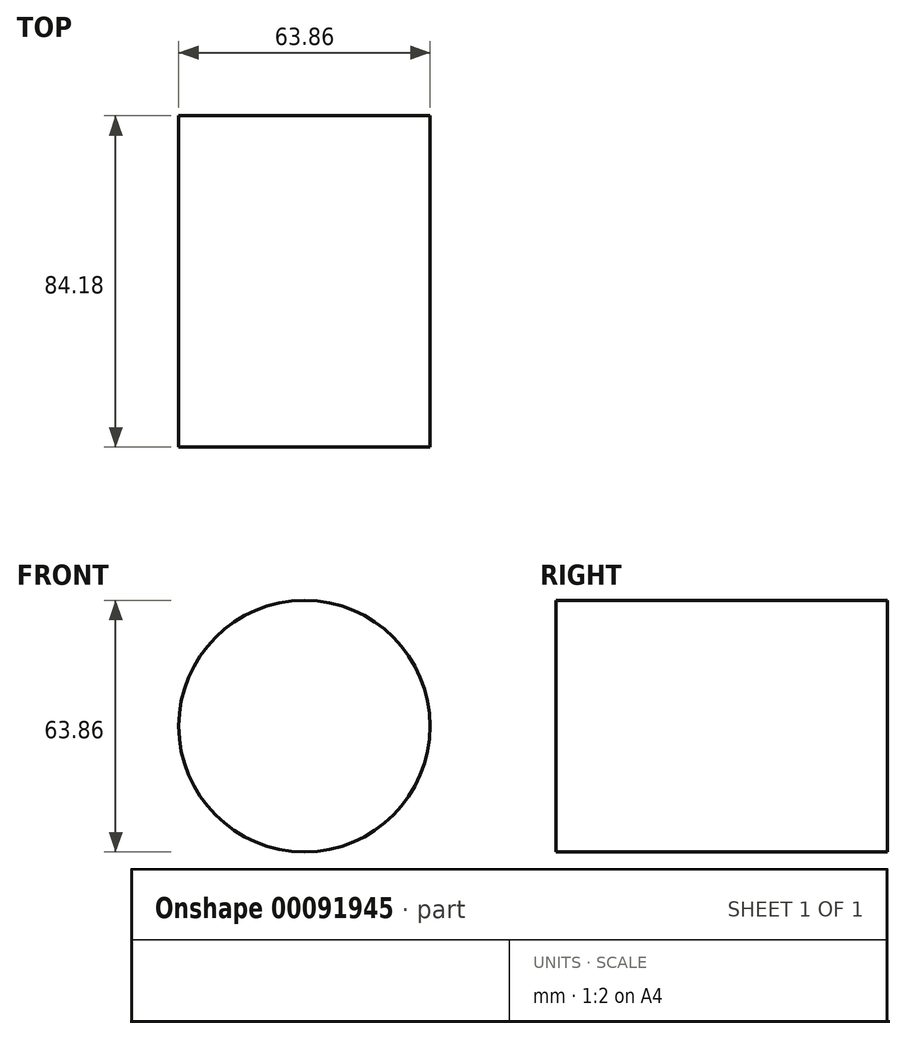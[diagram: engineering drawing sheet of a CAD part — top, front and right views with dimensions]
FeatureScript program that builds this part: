
annotation { "Feature Type Name" : "Feature", "Feature Type Description" : "" }
export const myFeature = defineFeature(function(context is Context, id is Id, definition is map)
    precondition{}
    {
        {
            var Q0;
            Q0=qCreatedBy(makeId("Front.planeOp"),FACE);
            var sketch = newSketch(context, id + "F0", { "sketchPlane" : qUnion([Q0])});
            skCircle(sketch, "E0", {"center": v(0, 0) * mm, "radius": 31.93 * mm});
            skSolve(sketch);
        }
        {
            var Q0;
            Q0=makeQuery(id+"F0.imprint","IMPRINT",FACE,{"disambiguationData":[TD([[makeQuery(id+"F0.imprint","IMPRINT",EDGE,{"derivedFrom":sQuery(id+"F0.wireOp",EDGE,"E0")}),1.0]])]});
            var Q1;
            Q1=sQuery(id+"F0.wireOp",EDGE,"E0");
            extrude(context, id + "F1", {"entities" : qUnion([Q0]), "bodyType" : ToolBodyType.SURFACE, "surfaceEntities" : qUnion([Q1]), "depth" : 84.18 * mm});
        }
    });
